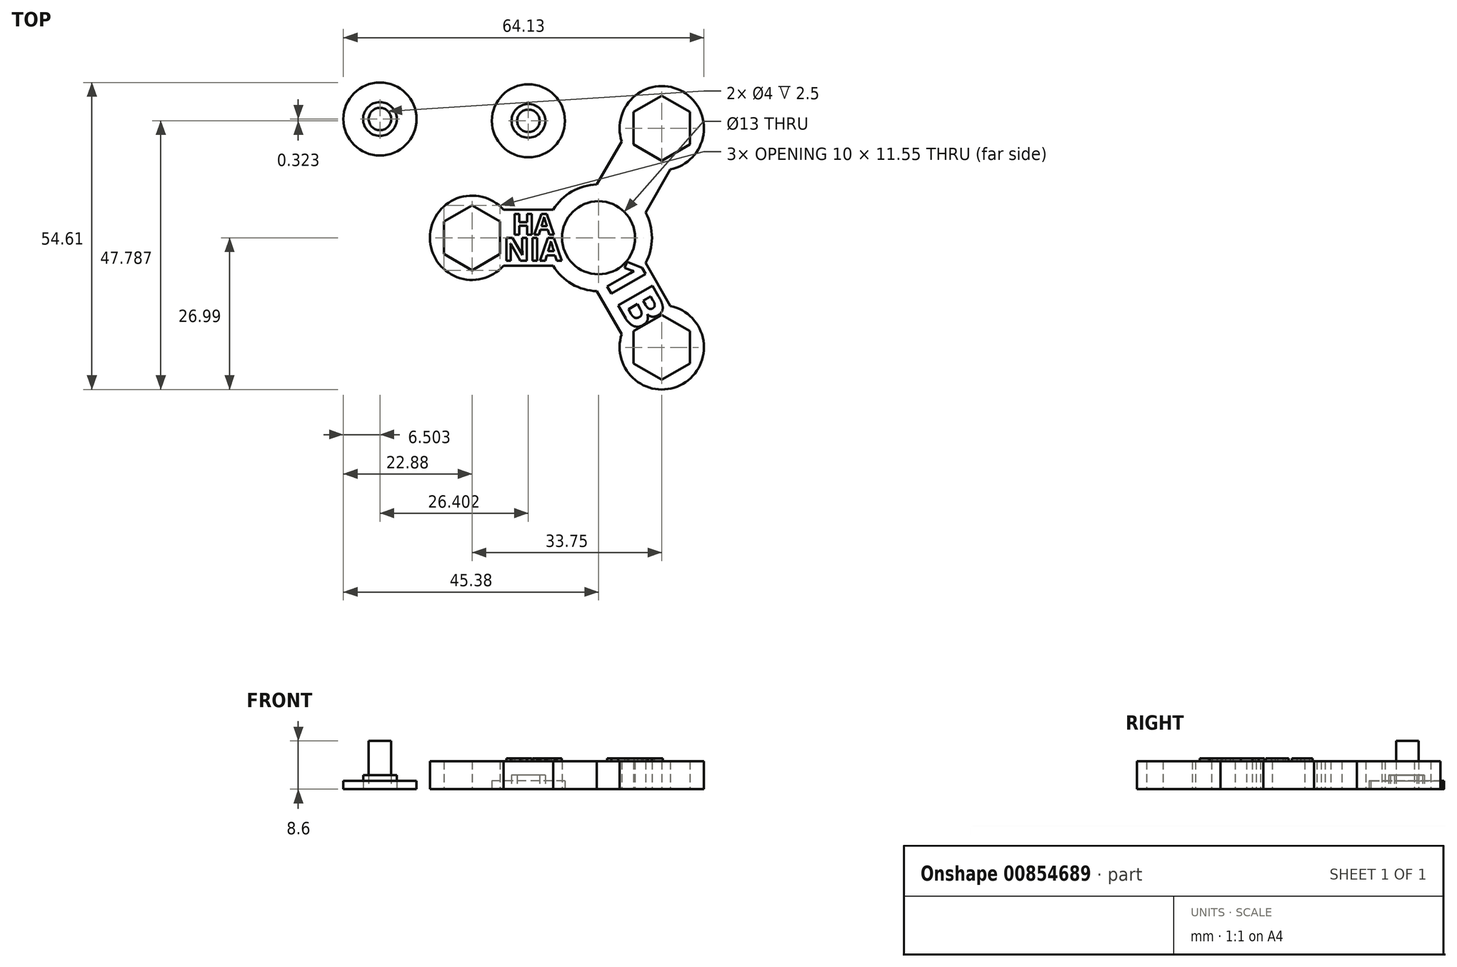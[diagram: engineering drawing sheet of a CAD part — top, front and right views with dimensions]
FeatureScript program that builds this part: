
annotation { "Feature Type Name" : "Feature", "Feature Type Description" : "" }
export const myFeature = defineFeature(function(context is Context, id is Id, definition is map)
    precondition{}
    {
        {
            var Q0;
            Q0=qCreatedBy(makeId("Top.planeOp"),FACE);
            var sketch = newSketch(context, id + "F0", { "sketchPlane" : qUnion([Q0])});
            skCircle(sketch, "E0", {"center": v(0, 0) * mm, "radius": 6.5 * mm});
            skCircle(sketch, "E1.cCircle", {"center": v(-22.5, 0) * mm, "radius": 5 * mm, "construction": true});
            skLineSegment(sketch, "E1.0", {"start": v(-27.5, -2.89) * mm, "end": v(-27.5, 2.89) * mm});
            skLineSegment(sketch, "E1.1", {"start": v(-27.5, 2.89) * mm, "end": v(-22.5, 5.77) * mm});
            skLineSegment(sketch, "E1.2", {"start": v(-22.5, 5.77) * mm, "end": v(-17.5, 2.89) * mm});
            skLineSegment(sketch, "E1.3", {"start": v(-17.5, 2.89) * mm, "end": v(-17.5, -2.89) * mm});
            skLineSegment(sketch, "E1.4", {"start": v(-17.5, -2.89) * mm, "end": v(-22.5, -5.77) * mm});
            skLineSegment(sketch, "E1.5", {"start": v(-22.5, -5.77) * mm, "end": v(-27.5, -2.89) * mm});
            skPoint(sketch, "E1.0.midPoint", {"position": v(-27.5, 0) * mm});
            skLineSegment(sketch, "E2", {"start": v(-8.08, 5) * mm, "end": v(-16.9, 5) * mm});
            skLineSegment(sketch, "E3", {"start": v(-8.08, -5) * mm, "end": v(-16.9, -5) * mm});
            skArc(sketch, "E4", {"start": v(-16.9, 5) * mm, "mid": v(-30, 0) * mm, "end": v(-16.9, -5) * mm});
            skLineSegment(sketch, "E5.1.0", {"start": v(16.25, -22.37) * mm, "end": v(11.25, -25.26) * mm});
            skLineSegment(sketch, "E5.1.2", {"start": v(8.37, -4.5) * mm, "end": v(12.79, -12.14) * mm});
            skLineSegment(sketch, "E5.1.3", {"start": v(11.25, -13.71) * mm, "end": v(16.25, -16.6) * mm});
            skArc(sketch, "E5.1.4", {"start": v(4.12, -17.14) * mm, "mid": v(15, -25.98) * mm, "end": v(12.79, -12.14) * mm});
            skLineSegment(sketch, "E5.1.5", {"start": v(16.25, -16.6) * mm, "end": v(16.25, -22.37) * mm});
            skPoint(sketch, "E5.1.6", {"position": v(13.75, -23.82) * mm});
            skLineSegment(sketch, "E5.1.7", {"start": v(6.25, -22.37) * mm, "end": v(6.25, -16.6) * mm});
            skCircle(sketch, "E5.1.8", {"center": v(11.25, -19.49) * mm, "radius": 5 * mm, "construction": true});
            skLineSegment(sketch, "E5.1.9", {"start": v(11.25, -25.26) * mm, "end": v(6.25, -22.37) * mm});
            skArc(sketch, "E5.1.10", {"start": v(8.37, -4.5) * mm, "mid": v(9.5, 0) * mm, "end": v(8.37, 4.5) * mm});
            skLineSegment(sketch, "E5.1.11", {"start": v(-0.3, -9.5) * mm, "end": v(-0.3, -9.5) * mm});
            skLineSegment(sketch, "E5.1.12", {"start": v(6.25, -16.6) * mm, "end": v(11.25, -13.71) * mm});
            skLineSegment(sketch, "E5.2.0", {"start": v(11.25, 25.26) * mm, "end": v(16.25, 22.37) * mm});
            skLineSegment(sketch, "E5.2.2", {"start": v(-0.3, 9.5) * mm, "end": v(4.12, 17.14) * mm});
            skLineSegment(sketch, "E5.2.3", {"start": v(6.25, 16.6) * mm, "end": v(6.25, 22.37) * mm});
            skArc(sketch, "E5.2.4", {"start": v(12.79, 12.14) * mm, "mid": v(15, 25.98) * mm, "end": v(4.12, 17.14) * mm});
            skLineSegment(sketch, "E5.2.5", {"start": v(6.25, 22.37) * mm, "end": v(11.25, 25.26) * mm});
            skPoint(sketch, "E5.2.6", {"position": v(13.75, 23.82) * mm});
            skLineSegment(sketch, "E5.2.7", {"start": v(16.25, 16.6) * mm, "end": v(11.25, 13.71) * mm});
            skCircle(sketch, "E5.2.8", {"center": v(11.25, 19.49) * mm, "radius": 5 * mm, "construction": true});
            skLineSegment(sketch, "E5.2.9", {"start": v(16.25, 22.37) * mm, "end": v(16.25, 16.6) * mm});
            skArc(sketch, "E5.2.10", {"start": v(-0.3, 9.5) * mm, "mid": v(-4.75, 8.23) * mm, "end": v(-8.08, 5) * mm});
            skLineSegment(sketch, "E5.2.11", {"start": v(8.37, 4.5) * mm, "end": v(12.79, 12.14) * mm});
            skLineSegment(sketch, "E5.2.12", {"start": v(11.25, 13.71) * mm, "end": v(6.25, 16.6) * mm});
            skArc(sketch, "E6", {"start": v(-8.08, -5) * mm, "mid": v(-4.75, -8.23) * mm, "end": v(-0.3, -9.5) * mm});
            skLineSegment(sketch, "E7", {"start": v(-0.3, -9.5) * mm, "end": v(4.12, -17.14) * mm});
            skLineSegment(sketch, "E8", {"start": v(8.37, -4.5) * mm, "end": v(8.37, -4.5) * mm});
            skText(sketch, "E9", { "text": "HA", "fontName": "OpenSans-Bold.ttf"});
            skText(sketch, "E10", { "text": "NIA", "fontName": "OpenSans-Bold.ttf"});
            skText(sketch, "E11", { "text": "1B", "fontName": "OpenSans-Bold.ttf"});
            const initialGuessF0  = {"E9": [-0.01535, 0.00057, 1, 0, 0.00368], "E10": [-0.01688, -0.00407, 1, 0, 0.00407], "E11": [0.00025, -0.0064, 0.5, -0.86603, 0.0071]};
            skSetInitialGuess(sketch, initialGuessF0);
            skSolve(sketch);
        }
        {
            var Q0;
            Q0 = qSketchRegion(id + "F0", true);
            var Q1;
            Q1=makeQuery(id+"F0.imprint","IMPRINT",FACE,{"disambiguationData":[TD([[makeQuery(id+"F0.imprint","IMPRINT",EDGE,{"derivedFrom":sQuery(id+"F0.wireOp",EDGE,"E11.sketch_text.stroke-10")}),-1.0]])]});
            var Q2;
            Q2=makeQuery(id+"F0.imprint","IMPRINT",FACE,{"disambiguationData":[TD([[makeQuery(id+"F0.imprint","IMPRINT",EDGE,{"derivedFrom":sQuery(id+"F0.wireOp",EDGE,"E11.sketch_text.stroke-29")}),1.0]])]});
            var Q3;
            Q3=makeQuery(id+"F0.imprint","IMPRINT",FACE,{"disambiguationData":[TD([[makeQuery(id+"F0.imprint","IMPRINT",EDGE,{"derivedFrom":sQuery(id+"F0.wireOp",EDGE,"E11.sketch_text.stroke-22")}),1.0]])]});
            var Q4;
            Q4=makeQuery(id+"F0.imprint","IMPRINT",FACE,{"disambiguationData":[TD([[makeQuery(id+"F0.imprint","IMPRINT",EDGE,{"derivedFrom":sQuery(id+"F0.wireOp",EDGE,"E11.sketch_text.stroke-0")}),-1.0]])]});
            var Q5;
            Q5=makeQuery(id+"F0.imprint","IMPRINT",FACE,{"disambiguationData":[TD([[makeQuery(id+"F0.imprint","IMPRINT",EDGE,{"derivedFrom":sQuery(id+"F0.wireOp",EDGE,"E10.sketch_text.stroke-18")}),-1.0]])]});
            var Q6;
            Q6=makeQuery(id+"F0.imprint","IMPRINT",FACE,{"disambiguationData":[TD([[makeQuery(id+"F0.imprint","IMPRINT",EDGE,{"derivedFrom":sQuery(id+"F0.wireOp",EDGE,"E10.sketch_text.stroke-14")}),-1.0]])]});
            var Q7;
            Q7=makeQuery(id+"F0.imprint","IMPRINT",FACE,{"disambiguationData":[TD([[makeQuery(id+"F0.imprint","IMPRINT",EDGE,{"derivedFrom":sQuery(id+"F0.wireOp",EDGE,"E10.sketch_text.stroke-26")}),1.0]])]});
            var Q8;
            Q8=makeQuery(id+"F0.imprint","IMPRINT",FACE,{"disambiguationData":[TD([[makeQuery(id+"F0.imprint","IMPRINT",EDGE,{"derivedFrom":sQuery(id+"F0.wireOp",EDGE,"E9.sketch_text.stroke-12")}),-1.0]])]});
            var Q9;
            Q9=makeQuery(id+"F0.imprint","IMPRINT",FACE,{"disambiguationData":[TD([[makeQuery(id+"F0.imprint","IMPRINT",EDGE,{"derivedFrom":sQuery(id+"F0.wireOp",EDGE,"E9.sketch_text.stroke-20")}),1.0]])]});
            var Q10;
            Q10=makeQuery(id+"F0.imprint","IMPRINT",FACE,{"disambiguationData":[TD([[makeQuery(id+"F0.imprint","IMPRINT",EDGE,{"derivedFrom":sQuery(id+"F0.wireOp",EDGE,"E9.sketch_text.stroke-0")}),-1.0]])]});
            var Q11;
            Q11=makeQuery(id+"F0.imprint","IMPRINT",FACE,{"disambiguationData":[TD([[makeQuery(id+"F0.imprint","IMPRINT",EDGE,{"derivedFrom":sQuery(id+"F0.wireOp",EDGE,"E10.sketch_text.stroke-0")}),-1.0]])]});
            extrude(context, id + "F1", {"entities" : qUnion([Q0, Q1, Q2, Q3, Q4, Q5, Q6, Q7, Q8, Q9, Q10, Q11]), "depth" : 5 * mm, "offsetDistance" : 25 * mm});
        }
        {
            var Q0;
            Q0=qCreatedBy(makeId("Top.planeOp"),FACE);
            var sketch = newSketch(context, id + "F2", { "sketchPlane" : qUnion([Q0])});
            skCircle(sketch, "E12", {"center": v(-12.48, 20.8) * mm, "radius": 6.5 * mm});
            skCircle(sketch, "E13", {"center": v(-38.88, 21.12) * mm, "radius": 6.5 * mm});
            skCircle(sketch, "E14", {"center": v(-38.88, 21.12) * mm, "radius": 3 * mm});
            skCircle(sketch, "E15", {"center": v(-12.48, 20.8) * mm, "radius": 3 * mm});
            skCircle(sketch, "E16", {"center": v(-38.88, 21.12) * mm, "radius": 2 * mm});
            skCircle(sketch, "E17", {"center": v(-12.48, 20.8) * mm, "radius": 2 * mm});
            skSolve(sketch);
        }
        {
            var Q0;
            Q0 = qSketchRegion(id + "F2", true);
            var Q1;
            Q1=makeQuery(id+"F2.imprint","IMPRINT",FACE,{"disambiguationData":[TD([[makeQuery(id+"F2.imprint","IMPRINT",EDGE,{"derivedFrom":sQuery(id+"F2.wireOp",EDGE,"E14")}),1.0]])]});
            var Q2;
            Q2=makeQuery(id+"F2.imprint","IMPRINT",FACE,{"disambiguationData":[TD([[makeQuery(id+"F2.imprint","IMPRINT",EDGE,{"derivedFrom":sQuery(id+"F2.wireOp",EDGE,"E16")}),1.0]])]});
            var Q3;
            Q3=makeQuery(id+"F2.imprint","IMPRINT",FACE,{"disambiguationData":[TD([[makeQuery(id+"F2.imprint","IMPRINT",EDGE,{"derivedFrom":sQuery(id+"F2.wireOp",EDGE,"E15")}),1.0]])]});
            var Q4;
            Q4=makeQuery(id+"F2.imprint","IMPRINT",FACE,{"disambiguationData":[TD([[makeQuery(id+"F2.imprint","IMPRINT",EDGE,{"derivedFrom":sQuery(id+"F2.wireOp",EDGE,"E17")}),1.0]])]});
            extrude(context, id + "F3", {"entities" : qUnion([Q0, Q1, Q2, Q3, Q4]), "depth" : 1.5 * mm, "offsetDistance" : 25 * mm});
        }
        {
            var Q0;
            Q0=makeQuery(id+"F2.imprint","IMPRINT",FACE,{"disambiguationData":[TD([[makeQuery(id+"F2.imprint","IMPRINT",EDGE,{"derivedFrom":sQuery(id+"F2.wireOp",EDGE,"E14")}),1.0]])]});
            var Q1;
            Q1=makeQuery(id+"F2.imprint","IMPRINT",FACE,{"disambiguationData":[TD([[makeQuery(id+"F2.imprint","IMPRINT",EDGE,{"derivedFrom":sQuery(id+"F2.wireOp",EDGE,"E15")}),1.0]])]});
            extrude(context, id + "F4", {"entities" : qUnion([Q0, Q1]), "depth" : 2.5 * mm, "offsetDistance" : 25 * mm});
        }
        {
            var Q0;
            Q0=makeQuery(id+"F2.imprint","IMPRINT",FACE,{"disambiguationData":[TD([[makeQuery(id+"F2.imprint","IMPRINT",EDGE,{"derivedFrom":sQuery(id+"F2.wireOp",EDGE,"E16")}),1.0]])]});
            extrude(context, id + "F5", {"entities" : qUnion([Q0]), "depth" : 8.6 * mm, "offsetDistance" : 25 * mm});
        }
        {
            var Q0;
            Q0=makeQuery(id+"F0.imprint","IMPRINT",FACE,{"disambiguationData":[TD([[makeQuery(id+"F0.imprint","IMPRINT",EDGE,{"derivedFrom":sQuery(id+"F0.wireOp",EDGE,"E10.sketch_text.stroke-0")}),-1.0]])]});
            var Q1;
            Q1=makeQuery(id+"F0.imprint","IMPRINT",FACE,{"disambiguationData":[TD([[makeQuery(id+"F0.imprint","IMPRINT",EDGE,{"derivedFrom":sQuery(id+"F0.wireOp",EDGE,"E10.sketch_text.stroke-14")}),-1.0]])]});
            var Q2;
            Q2=makeQuery(id+"F0.imprint","IMPRINT",FACE,{"disambiguationData":[TD([[makeQuery(id+"F0.imprint","IMPRINT",EDGE,{"derivedFrom":sQuery(id+"F0.wireOp",EDGE,"E10.sketch_text.stroke-18")}),-1.0]])]});
            var Q3;
            Q3=makeQuery(id+"F0.imprint","IMPRINT",FACE,{"disambiguationData":[TD([[makeQuery(id+"F0.imprint","IMPRINT",EDGE,{"derivedFrom":sQuery(id+"F0.wireOp",EDGE,"E9.sketch_text.stroke-12")}),-1.0]])]});
            var Q4;
            Q4=makeQuery(id+"F0.imprint","IMPRINT",FACE,{"disambiguationData":[TD([[makeQuery(id+"F0.imprint","IMPRINT",EDGE,{"derivedFrom":sQuery(id+"F0.wireOp",EDGE,"E9.sketch_text.stroke-0")}),-1.0]])]});
            var Q5;
            Q5=makeQuery(id+"F0.imprint","IMPRINT",FACE,{"disambiguationData":[TD([[makeQuery(id+"F0.imprint","IMPRINT",EDGE,{"derivedFrom":sQuery(id+"F0.wireOp",EDGE,"E11.sketch_text.stroke-0")}),-1.0]])]});
            var Q6;
            Q6=makeQuery(id+"F0.imprint","IMPRINT",FACE,{"disambiguationData":[TD([[makeQuery(id+"F0.imprint","IMPRINT",EDGE,{"derivedFrom":sQuery(id+"F0.wireOp",EDGE,"E11.sketch_text.stroke-10")}),-1.0]])]});
            extrude(context, id + "F6", {"entities" : qUnion([Q0, Q1, Q2, Q3, Q4, Q5, Q6]), "operationType" : NewBodyOperationType.ADD, "depth" : 5.5 * mm, "offsetDistance" : 25 * mm});
        }
    });
